# Revit family: BOS-Renovierungszarge-wkUud_Familie
name_source: partatom
category: Türen
revit_build: Autodesk Revit 2017 (Build: 20160225_1515(x64)
units: mm (PartAtom-declared; Revit-internal decimal feet)

## family parameters
Basisbauteil = Wand
Beim Laden mit Abzugskörper schneiden = Nein
Gemeinsam genutzt = Nein
Immer vertikal = Ja
Raumberechnungspunkt = Ja

## types (4) — shared parameters
Allgemeine Informationen zu Stahlzargen = www.BestOfSteel.de/tools-downloads/technische-infos-rund-um-die-stahlzarge/
BBL1 Bandbezugslinie   Hinge Position 1 = 241 mm  [stored 0.790682 ft]
BE max. = 100 mm  [stored 0.328084 ft]
Bauelement = BOS Stahlzarge
Dichtung 1 = Ja
Doppelfalz = Nein
Einfachfalz = Ja
FMB max. = 1341 mm  [stored 4.39961 ft]
FMB min. = 591 mm  [stored 1.93898 ft]
FMH max. = 2858 mm  [stored 9.37664 ft]
FMH min. = 1608 mm  [stored 5.27559 ft]
Falzaufschlag = 15 mm  [stored 0.0492126 ft]
Falzaufschlag gesamt = 15 mm  [stored 0.0492126 ft]
Falztiefe 2 = 25 mm  [stored 0.082021 ft]
Funktion = Innen
GT max. = 650 mm  [stored 2.13255 ft]
Hersteller = BOS GmbH Best Of Steel, Lütkenfelde 4, D-48282 Emsdetten
Info-Texte sichtbar = Ja
Information in English = Nein
Material = grundiert, feuerverzinktes Feinblech nach DIN EN 10143
Material - Bänder = <Nach Kategorie>
Material - Dichtung = <Nach Kategorie>
Material - Drückergarnitur = <Nach Kategorie>
Material - Türblatt = <Nach Kategorie>
Material - Zarge = <Nach Kategorie>
Türblattstärke = 40 mm  [stored 0.131234 ft]
URL = www.BestOfSteel.de/stahlzargen/zargen-fuer-drehfluegeltueren/2-schalige-stahlzargen/2-schalige-renovierungszargen/
zero-valued in all types: Breite, Dicke, Rohbaubreite, Rohbauhöhe, Türblattstärke 3

## per-type parameters (varying)
| type | Beschreibung | Einfügepunkt | Falztiefe | Falztiefe gesamt | Gefälzt | MW min. | Stumpf | Türblattstärke 1 | Türblattstärke 2 | Umgedreht | wkUsd | wkUsd (umgedreht) | wkUud | wkUud (umgedreht) |
| wkUud (Umgedreht) | 2-schalige Umfassungszarge über vorhandene Zarge, mit Verstellbereich, gefälzt | 9.5 mm  [stored 0.031168 ft] | 28.5 mm  [stored 0.0935039 ft] | 28.5 mm  [stored 0.0935039 ft] | Ja | 100 mm  [stored 0.328084 ft] | Nein | 14.5 mm  [stored 0.0475722 ft] | 25.5 mm | Ja | Nein | Nein | Nein | Ja |
| wkUud | 2-schalige Umfassungszarge über vorhandene Zarge, mit Verstellbereich, gefälzt | 12 mm  [stored 0.0393701 ft] | 28.5 mm  [stored 0.0935039 ft] | 28.5 mm  [stored 0.0935039 ft] | Ja | 100 mm  [stored 0.328084 ft] | Nein | 14.5 mm  [stored 0.0475722 ft] | 25.5 mm | Nein | Nein | Nein | Ja | Nein |
| wkUsd (Umgedreht) | 2-schalige Umfassungszarge über vorhandene Zarge, mit Verstellbereich, stumpf | 9.5 mm  [stored 0.031168 ft] | 46.5 mm  [stored 0.152559 ft] | 46.5 mm  [stored 0.152559 ft] | Nein | 125 mm  [stored 0.410105 ft] | Ja | 0 mm  [stored 0 ft] | 40 mm  [stored 0.131234 ft] | Ja | Nein | Ja | Nein | Nein |
| wkUsd | 2-schalige Umfassungszarge über vorhandene Zarge, mit Verstellbereich, stumpf | 12 mm  [stored 0.0393701 ft] | 46.5 mm  [stored 0.152559 ft] | 46.5 mm  [stored 0.152559 ft] | Nein | 125 mm  [stored 0.410105 ft] | Ja | 0 mm  [stored 0 ft] | 40 mm  [stored 0.131234 ft] | Nein | Ja | Nein | Nein | Nein |

note: column(s) folded — value = type name in every type: Modell

note: [stored X ft] marks values corroborated as IEEE doubles in the binary element streams (Revit-internal decimal feet)
